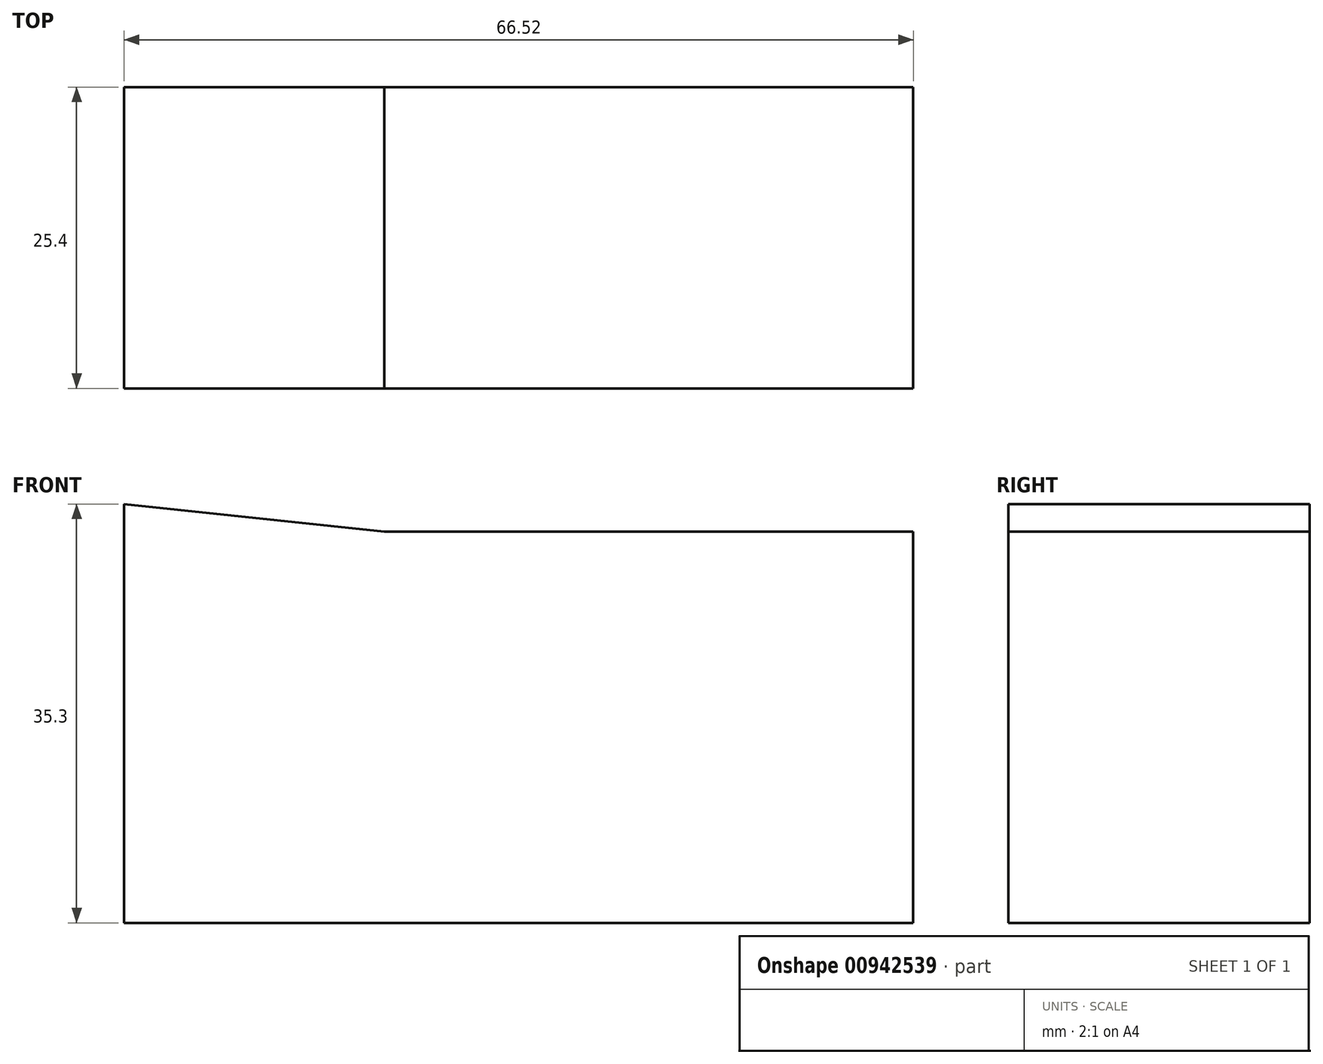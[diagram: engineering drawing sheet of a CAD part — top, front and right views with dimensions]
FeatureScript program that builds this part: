
annotation { "Feature Type Name" : "Feature", "Feature Type Description" : "" }
export const myFeature = defineFeature(function(context is Context, id is Id, definition is map)
    precondition{}
    {
        {
            var Q0;
            Q0=qCreatedBy(makeId("Front.planeOp"),FACE);
            var sketch = newSketch(context, id + "F0", { "sketchPlane" : qUnion([Q0])});
            skLineSegment(sketch, "E0.bottom", {"start": v(-25.08, 32.97) * mm, "end": v(-3.58, 32.97) * mm});
            skLineSegment(sketch, "E0.top", {"start": v(-25.08, 0) * mm, "end": v(-3.58, 0) * mm});
            skLineSegment(sketch, "E0.left", {"start": v(-25.08, 32.97) * mm, "end": v(-25.08, 0) * mm});
            skLineSegment(sketch, "E0.right", {"start": v(-3.58, 32.97) * mm, "end": v(-3.58, 0) * mm});
            skLineSegment(sketch, "E1.bottom", {"start": v(-3.58, 0) * mm, "end": v(19.52, 0) * mm});
            skLineSegment(sketch, "E1.top", {"start": v(-3.58, 6.22) * mm, "end": v(19.52, 6.22) * mm});
            skLineSegment(sketch, "E1.left", {"start": v(-3.58, 0) * mm, "end": v(-3.58, 6.22) * mm});
            skLineSegment(sketch, "E1.right", {"start": v(19.52, 0) * mm, "end": v(19.52, 6.22) * mm});
            skLineSegment(sketch, "E2.bottom", {"start": v(-25.08, 0) * mm, "end": v(-47, 0) * mm});
            skLineSegment(sketch, "E2.top", {"start": v(-25.08, 6.18) * mm, "end": v(-47, 6.18) * mm});
            skLineSegment(sketch, "E2.left", {"start": v(-25.08, 0) * mm, "end": v(-25.08, 6.18) * mm});
            skLineSegment(sketch, "E2.right", {"start": v(-47, 0) * mm, "end": v(-47, 6.18) * mm});
            skLineSegment(sketch, "E3", {"start": v(-47, 6.18) * mm, "end": v(-47, 35.3) * mm});
            skLineSegment(sketch, "E4", {"start": v(-47, 35.3) * mm, "end": v(-25.08, 32.97) * mm});
            skLineSegment(sketch, "E5", {"start": v(19.52, 6.22) * mm, "end": v(19.52, 32.97) * mm});
            skLineSegment(sketch, "E6", {"start": v(-3.58, 32.97) * mm, "end": v(19.52, 32.97) * mm});
            skSolve(sketch);
        }
        {
            var Q0;
            Q0=qCreatedBy(makeId("Top.planeOp"),FACE);
            var sketch = newSketch(context, id + "F1", { "sketchPlane" : qUnion([Q0])});
            skSolve(sketch);
        }
        {
            var Q0;
            Q0 = qSketchRegion(id + "F1", true);
            var Q1;
            Q1=makeQuery(id+"F0.imprint","IMPRINT",FACE,{"disambiguationData":[TD([[makeQuery(id+"F0.imprint","IMPRINT",EDGE,{"derivedFrom":sQuery(id+"F0.wireOp",EDGE,"E0.left")}),-1.0]])]});
            var Q2;
            Q2=makeQuery(id+"F0.imprint","IMPRINT",FACE,{"disambiguationData":[TD([[makeQuery(id+"F0.imprint","IMPRINT",EDGE,{"derivedFrom":sQuery(id+"F0.wireOp",EDGE,"E0.bottom")}),-1.0]])]});
            var Q3;
            Q3=makeQuery(id+"F0.imprint","IMPRINT",FACE,{"disambiguationData":[TD([[makeQuery(id+"F0.imprint","IMPRINT",EDGE,{"derivedFrom":sQuery(id+"F0.wireOp",EDGE,"E2.bottom")}),-1.0]])]});
            var Q4;
            Q4=makeQuery(id+"F0.imprint","IMPRINT",FACE,{"disambiguationData":[TD([[makeQuery(id+"F0.imprint","IMPRINT",EDGE,{"derivedFrom":sQuery(id+"F0.wireOp",EDGE,"E1.bottom")}),1.0]])]});
            var Q5;
            Q5=makeQuery(id+"F0.imprint","IMPRINT",FACE,{"disambiguationData":[TD([[makeQuery(id+"F0.imprint","IMPRINT",EDGE,{"derivedFrom":sQuery(id+"F0.wireOp",EDGE,"E0.right")}),1.0]])]});
            extrude(context, id + "F2", {"entities" : qUnion([Q0, Q1, Q2, Q3, Q4, Q5]), "depth" : 25.4 * mm, "offsetDistance" : 25.4 * mm});
        }
    });
